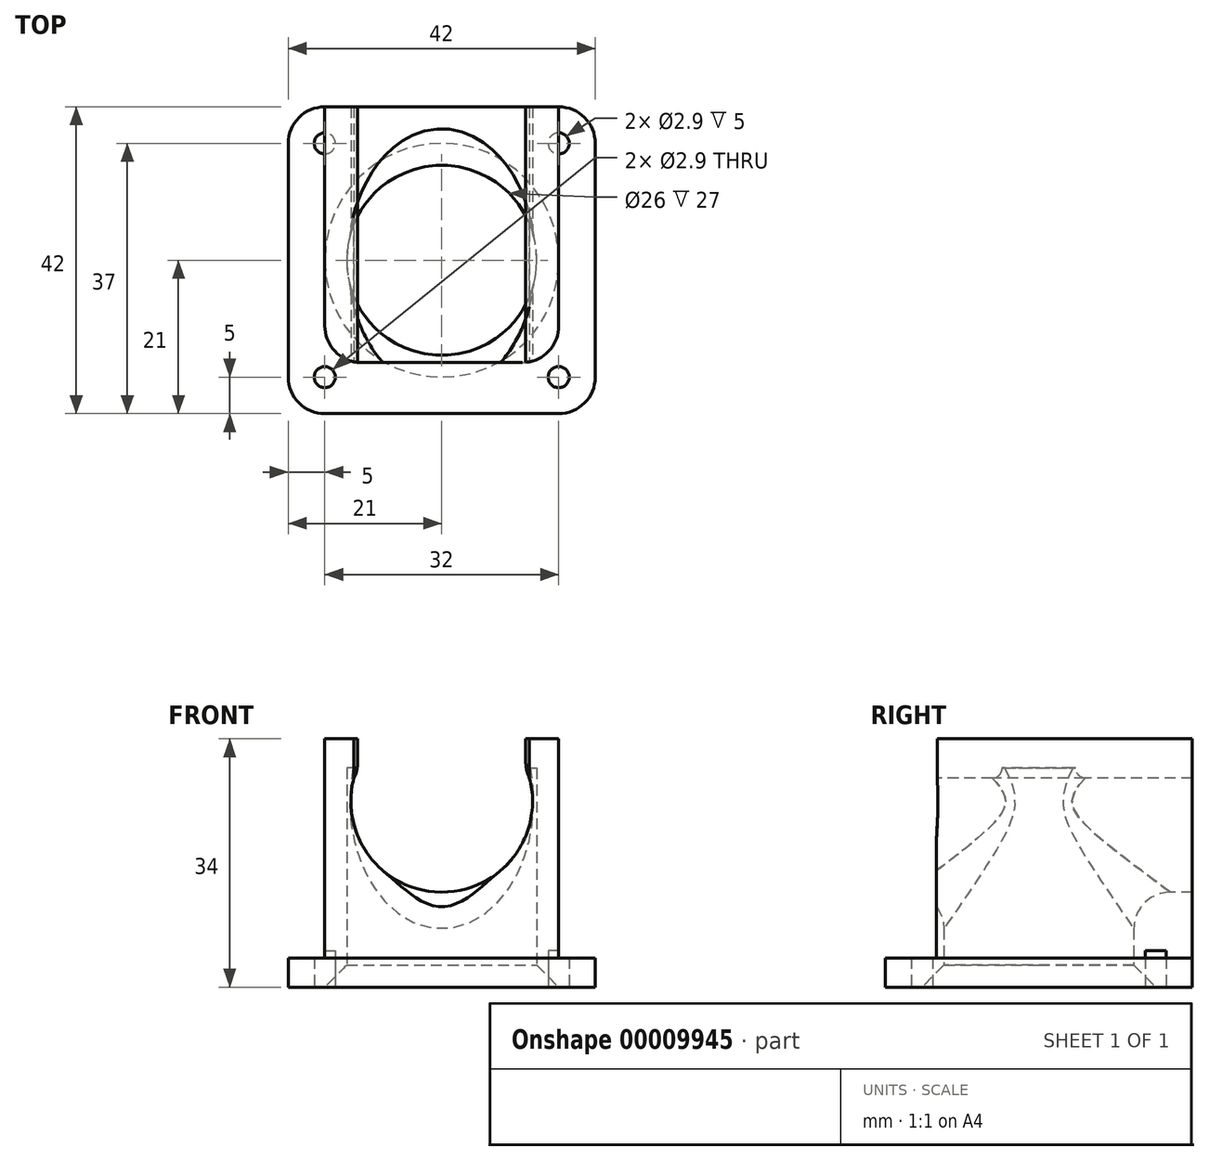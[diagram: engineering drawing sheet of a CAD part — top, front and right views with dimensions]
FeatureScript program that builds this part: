
annotation { "Feature Type Name" : "Feature", "Feature Type Description" : "" }
export const myFeature = defineFeature(function(context is Context, id is Id, definition is map)
    precondition{}
    {
        {
            var Q0;
            Q0=qCreatedBy(makeId("Top.planeOp"),FACE);
            var sketch = newSketch(context, id + "F0", { "sketchPlane" : qUnion([Q0])});
            skLineSegment(sketch, "E0.bottom", {"start": v(0, 0) * mm, "end": v(42, 0) * mm});
            skLineSegment(sketch, "E0.top", {"start": v(0, 42) * mm, "end": v(42, 42) * mm});
            skLineSegment(sketch, "E0.left", {"start": v(0, 0) * mm, "end": v(0, 42) * mm});
            skLineSegment(sketch, "E0.right", {"start": v(42, 0) * mm, "end": v(42, 42) * mm});
            skSolve(sketch);
        }
        {
            var Q0;
            Q0=qSketchRegion(id+"F0",true);
            extrude(context, id + "F1", {"entities" : qUnion([Q0]), "depth" : 4 * mm});
        }
        {
            var Q0;
            Q0=makeQuery(id+"F1.opExtrude","CAP_FACE",FACE,{"disambiguationData":[OSD([sQuery(id+"F0.wireOp",EDGE,"E0.bottom"),sQuery(id+"F0.wireOp",EDGE,"E0.top"),sQuery(id+"F0.wireOp",EDGE,"E0.left"),sQuery(id+"F0.wireOp",EDGE,"E0.right")])],"isStart":false});
            var sketch = newSketch(context, id + "F2", { "sketchPlane" : qUnion([Q0])});
            skLineSegment(sketch, "E1.bottom", {"start": v(5, 42) * mm, "end": v(37, 42) * mm});
            skLineSegment(sketch, "E1.top", {"start": v(5, 7) * mm, "end": v(37, 7) * mm});
            skLineSegment(sketch, "E1.left", {"start": v(5, 42) * mm, "end": v(5, 7) * mm});
            skLineSegment(sketch, "E1.right", {"start": v(37, 42) * mm, "end": v(37, 7) * mm});
            skLineSegment(sketch, "E2", {"start": v(37, 21) * mm, "end": v(42, 21) * mm});
            skLineSegment(sketch, "E3", {"start": v(5, 19.4) * mm, "end": v(0, 19.4) * mm});
            skSolve(sketch);
        }
        {
            var Q0;
            Q0=qSketchRegion(id+"F2",true);
            extrude(context, id + "F3", {"entities" : qUnion([Q0]), "operationType" : NewBodyOperationType.ADD, "depth" : 30 * mm});
        }
        {
            var Q0;
            Q0=makeQuery(id+"F1.opExtrude","CAP_FACE",FACE,{"disambiguationData":[OSD([sQuery(id+"F0.wireOp",EDGE,"E0.bottom"),sQuery(id+"F0.wireOp",EDGE,"E0.top"),sQuery(id+"F0.wireOp",EDGE,"E0.left"),sQuery(id+"F0.wireOp",EDGE,"E0.right")])],"isStart":true});
            var sketch = newSketch(context, id + "F4", { "sketchPlane" : qUnion([Q0])});
            skCircle(sketch, "E4", {"center": v(21, -21) * mm, "radius": 19 * mm});
            skLineSegment(sketch, "E5", {"start": v(21, -21) * mm, "end": v(21, 0) * mm});
            skLineSegment(sketch, "E6", {"start": v(21, -21) * mm, "end": v(42, -21) * mm});
            skSolve(sketch);
        }
        {
            var Q0;
            Q0=qSketchRegion(id+"F4",true);
            extrude(context, id + "F5", {"entities" : qUnion([Q0]), "operationType" : NewBodyOperationType.REMOVE, "oppositeDirection" : true, "depth" : 3 * mm});
        }
        {
            var Q0;
            Q0=makeQuery(id+"F5.boolean.opBoolean","COPY",FACE,{"derivedFrom":makeQuery(id+"F5.opExtrude","CAP_FACE",FACE,{"disambiguationData":[OSD([sQuery(id+"F4.wireOp",EDGE,"E4")])],"isStart":false})});
            var sketch = newSketch(context, id + "F6", { "sketchPlane" : qUnion([Q0])});
            skCircle(sketch, "E7", {"center": v(21, -21) * mm, "radius": 13 * mm});
            skSolve(sketch);
        }
        {
            var Q0;
            Q0=qSketchRegion(id+"F6",true);
            extrude(context, id + "F7", {"entities" : qUnion([Q0]), "operationType" : NewBodyOperationType.REMOVE, "oppositeDirection" : true, "depth" : 27 * mm});
        }
        {
            var Q0;
            Q0=makeQuery(id+"F3.opExtrude","SWEPT_FACE",FACE,{"disambiguationData":[OSD([sQuery(id+"F2.wireOp",EDGE,"E1.top")])]});
            var sketch = newSketch(context, id + "F8", { "sketchPlane" : qUnion([Q0])});
            skLineSegment(sketch, "E8", {"start": v(9, 34) * mm, "end": v(9, 28.62) * mm});
            skLineSegment(sketch, "E9", {"start": v(33, 34) * mm, "end": v(33, 28.62) * mm});
            skLineSegment(sketch, "E10", {"start": v(9, 28.62) * mm, "end": v(5, 28.62) * mm, "construction": true});
            skLineSegment(sketch, "E11", {"start": v(33, 28.62) * mm, "end": v(37, 28.62) * mm, "construction": true});
            skCircle(sketch, "E12", {"center": v(21, 25.42) * mm, "radius": 12.42 * mm});
            skSolve(sketch);
        }
        {
            var Q0;
            Q0=qSketchRegion(id+"F8",true);
            var Q1;
            {var subQ3=sQuery(id+"F8.wireOp",EDGE,"E8");Q1=makeQuery(id+"F8.imprint","IMPRINT",FACE,{"disambiguationData":[TD([[makeQuery(id+"F8.imprint","IMPRINT",EDGE,{"derivedFrom":subQ3}),1.0]])]});}
            var Q2;
            {var subQ3=sQuery(id+"F8.wireOp",EDGE,"E9");Q2=makeQuery(id+"F8.imprint","IMPRINT",FACE,{"disambiguationData":[TD([[makeQuery(id+"F8.imprint","IMPRINT",EDGE,{"derivedFrom":subQ3}),-1.0]])]});}
            extrude(context, id + "F9", {"entities" : qUnion([Q0, Q1, Q2]), "operationType" : NewBodyOperationType.REMOVE, "endBound" : BoundingType.THROUGH_ALL, "oppositeDirection" : true, "depth" : 25 * mm});
        }
        {
            var Q0;
            Q0=makeQuery(id+"F1.opExtrude","SWEPT_EDGE",EDGE,{"disambiguationData":[OSD([sQuery(id+"F0.wireOp",EDGE,"E0.top"),sQuery(id+"F0.wireOp",EDGE,"E0.right")])]});
            var Q1;
            Q1=makeQuery(id+"F1.opExtrude","SWEPT_EDGE",EDGE,{"disambiguationData":[OSD([sQuery(id+"F0.wireOp",EDGE,"E0.top"),sQuery(id+"F0.wireOp",EDGE,"E0.left")])]});
            var Q2;
            Q2=makeQuery(id+"F1.opExtrude","SWEPT_EDGE",EDGE,{"disambiguationData":[OSD([sQuery(id+"F0.wireOp",EDGE,"E0.bottom"),sQuery(id+"F0.wireOp",EDGE,"E0.left")])]});
            var Q3;
            Q3=makeQuery(id+"F1.opExtrude","SWEPT_EDGE",EDGE,{"disambiguationData":[OSD([sQuery(id+"F0.wireOp",EDGE,"E0.bottom"),sQuery(id+"F0.wireOp",EDGE,"E0.right")])]});
            fillet(context, id + "F10", {"entities" : qUnion([Q0, Q1, Q2, Q3]), "radius" : 5 * mm, "tangentPropagation" : true, "allowEdgeOverflow" : false});
        }
        {
            var Q0;
            Q0=makeQuery(id+"F3.opExtrude","SWEPT_EDGE",EDGE,{"disambiguationData":[OSD([sQuery(id+"F2.wireOp",EDGE,"E1.top"),sQuery(id+"F2.wireOp",EDGE,"E1.left")])]});
            var Q1;
            Q1=makeQuery(id+"F3.opExtrude","SWEPT_EDGE",EDGE,{"disambiguationData":[OSD([sQuery(id+"F2.wireOp",EDGE,"E1.top"),sQuery(id+"F2.wireOp",EDGE,"E1.right")])]});
            var Q2;
            Q2=makeQuery(id+"F10.opFillet","BLEND_EDGE",EDGE,{"blendedFrom":[makeQuery(id+"F1.opExtrude","SWEPT_EDGE",EDGE,{"disambiguationData":[OSD([sQuery(id+"F0.wireOp",EDGE,"E0.bottom"),sQuery(id+"F0.wireOp",EDGE,"E0.right")])]}),makeQuery(id+"F3.opExtrude","SWEPT_FACE",FACE,{"disambiguationData":[OSD([sQuery(id+"F2.wireOp",EDGE,"E1.right")])]})],"blendedInto":[makeQuery(id+"F3.opExtrude","SWEPT_FACE",FACE,{"disambiguationData":[OSD([sQuery(id+"F2.wireOp",EDGE,"E1.right")])]})]});
            fillet(context, id + "F11", {"entities" : qUnion([Q0, Q1, Q2]), "radius" : 5 * mm, "tangentPropagation" : true, "allowEdgeOverflow" : false});
        }
        {
            var Q0;
            {var subQ0=sQuery(id+"F8.wireOp",EDGE,"E12");Q0=makeQuery(id+"F9.boolean.opBoolean","INTERSECT",EDGE,{"derivedFrom":[makeQuery(id+"F7.boolean.opBoolean","COPY",FACE,{"derivedFrom":makeQuery(id+"F7.opExtrude","SWEPT_FACE",FACE,{"disambiguationData":[OSD([sQuery(id+"F6.wireOp",EDGE,"E7")])]})}),makeQuery(id+"F9.opExtrude","SWEPT_FACE",FACE,{"disambiguationData":[OSD([subQ0]),TDD([makeQuery(id+"F8.imprint","IMPRINT",EDGE,{"disambiguationData":[TD([[makeQuery(id+"F8.imprint","INTERSECT",VERTEX,{"derivedFrom":[sQuery(id+"F8.wireOp",EDGE,"E8"),subQ0]}),-1.0]])],"derivedFrom":subQ0})])]})]});}
            fillet(context, id + "F12", {"entities" : qUnion([Q0]), "radius" : 5 * mm, "tangentPropagation" : true, "allowEdgeOverflow" : false});
        }
        {
            var Q0;
            Q0=makeQuery(id+"F1.opExtrude","CAP_FACE",FACE,{"disambiguationData":[OSD([sQuery(id+"F0.wireOp",EDGE,"E0.bottom"),sQuery(id+"F0.wireOp",EDGE,"E0.top"),sQuery(id+"F0.wireOp",EDGE,"E0.left"),sQuery(id+"F0.wireOp",EDGE,"E0.right")])],"isStart":true});
            var sketch = newSketch(context, id + "F13", { "sketchPlane" : qUnion([Q0])});
            skCircle(sketch, "E13", {"center": v(5, -5) * mm, "radius": 1.45 * mm});
            skCircle(sketch, "E14", {"center": v(37, -5) * mm, "radius": 1.45 * mm});
            skCircle(sketch, "E15", {"center": v(37, -37) * mm, "radius": 1.45 * mm});
            skCircle(sketch, "E16", {"center": v(5, -37) * mm, "radius": 1.45 * mm});
            skSolve(sketch);
        }
        {
            var Q0;
            Q0=qSketchRegion(id+"F13",true);
            extrude(context, id + "F14", {"entities" : qUnion([Q0]), "operationType" : NewBodyOperationType.REMOVE, "oppositeDirection" : true, "depth" : 5 * mm});
        }
        {
            var Q0;
            Q0=makeQuery(id+"F5.boolean.opBoolean","COPY",EDGE,{"derivedFrom":makeQuery(id+"F5.opExtrude","CAP_EDGE",EDGE,{"disambiguationData":[OSD([sQuery(id+"F4.wireOp",EDGE,"E4")])],"isStart":false})});
            chamfer(context, id + "F15", {"entities" : qUnion([Q0]), "width" : 6 * mm, "tangentPropagation" : true});
        }
        {
            var Q0;
            Q0=makeQuery(id+"F9.boolean.opBoolean","COPY",FACE,{"derivedFrom":makeQuery(id+"F9.opExtrude","SWEPT_FACE",FACE,{"disambiguationData":[OSD([sQuery(id+"F8.wireOp",EDGE,"E8")])]})});
            var sketch = newSketch(context, id + "F16", { "sketchPlane" : qUnion([Q0])});
            skLineSegment(sketch, "E17.bottom", {"start": v(7.1, 34) * mm, "end": v(42, 34) * mm});
            skLineSegment(sketch, "E17.top", {"start": v(7.1, 28.62) * mm, "end": v(42, 28.62) * mm});
            skLineSegment(sketch, "E17.left", {"start": v(7.1, 34) * mm, "end": v(7.1, 28.62) * mm});
            skLineSegment(sketch, "E17.right", {"start": v(42, 34) * mm, "end": v(42, 28.62) * mm});
            skSolve(sketch);
        }
        {
            var Q0;
            Q0 = qSketchRegion(id + "F16", true);
            extrude(context, id + "F17", {"entities" : qUnion([Q0]), "operationType" : NewBodyOperationType.ADD, "depth" : 0.5 * mm});
        }
        {
            var Q0;
            Q0=makeQuery(id+"F9.boolean.opBoolean","COPY",FACE,{"derivedFrom":makeQuery(id+"F9.opExtrude","SWEPT_FACE",FACE,{"disambiguationData":[OSD([sQuery(id+"F8.wireOp",EDGE,"E9")])]})});
            var sketch = newSketch(context, id + "F18", { "sketchPlane" : qUnion([Q0])});
            skLineSegment(sketch, "E18.bottom", {"start": v(-42, 34) * mm, "end": v(-7.1, 34) * mm});
            skLineSegment(sketch, "E18.top", {"start": v(-42, 28.62) * mm, "end": v(-7.1, 28.62) * mm});
            skLineSegment(sketch, "E18.left", {"start": v(-42, 34) * mm, "end": v(-42, 28.62) * mm});
            skLineSegment(sketch, "E18.right", {"start": v(-7.1, 34) * mm, "end": v(-7.1, 28.62) * mm});
            skSolve(sketch);
        }
        {
            var Q0;
            Q0 = qSketchRegion(id + "F18", true);
            extrude(context, id + "F19", {"entities" : qUnion([Q0]), "operationType" : NewBodyOperationType.ADD, "depth" : 0.5 * mm});
        }
        {
            var Q0;
            Q0=makeQuery(id+"F19.opExtrude","CAP_EDGE",EDGE,{"disambiguationData":[OSD([sQuery(id+"F18.wireOp",EDGE,"E18.top")])],"isStart":false});
            var Q1;
            Q1=makeQuery(id+"F17.opExtrude","CAP_EDGE",EDGE,{"disambiguationData":[OSD([sQuery(id+"F16.wireOp",EDGE,"E17.top")])],"isStart":false});
            fillet(context, id + "F20", {"entities" : qUnion([Q0, Q1]), "radius" : 5 * mm, "tangentPropagation" : true, "allowEdgeOverflow" : false});
        }
    });
